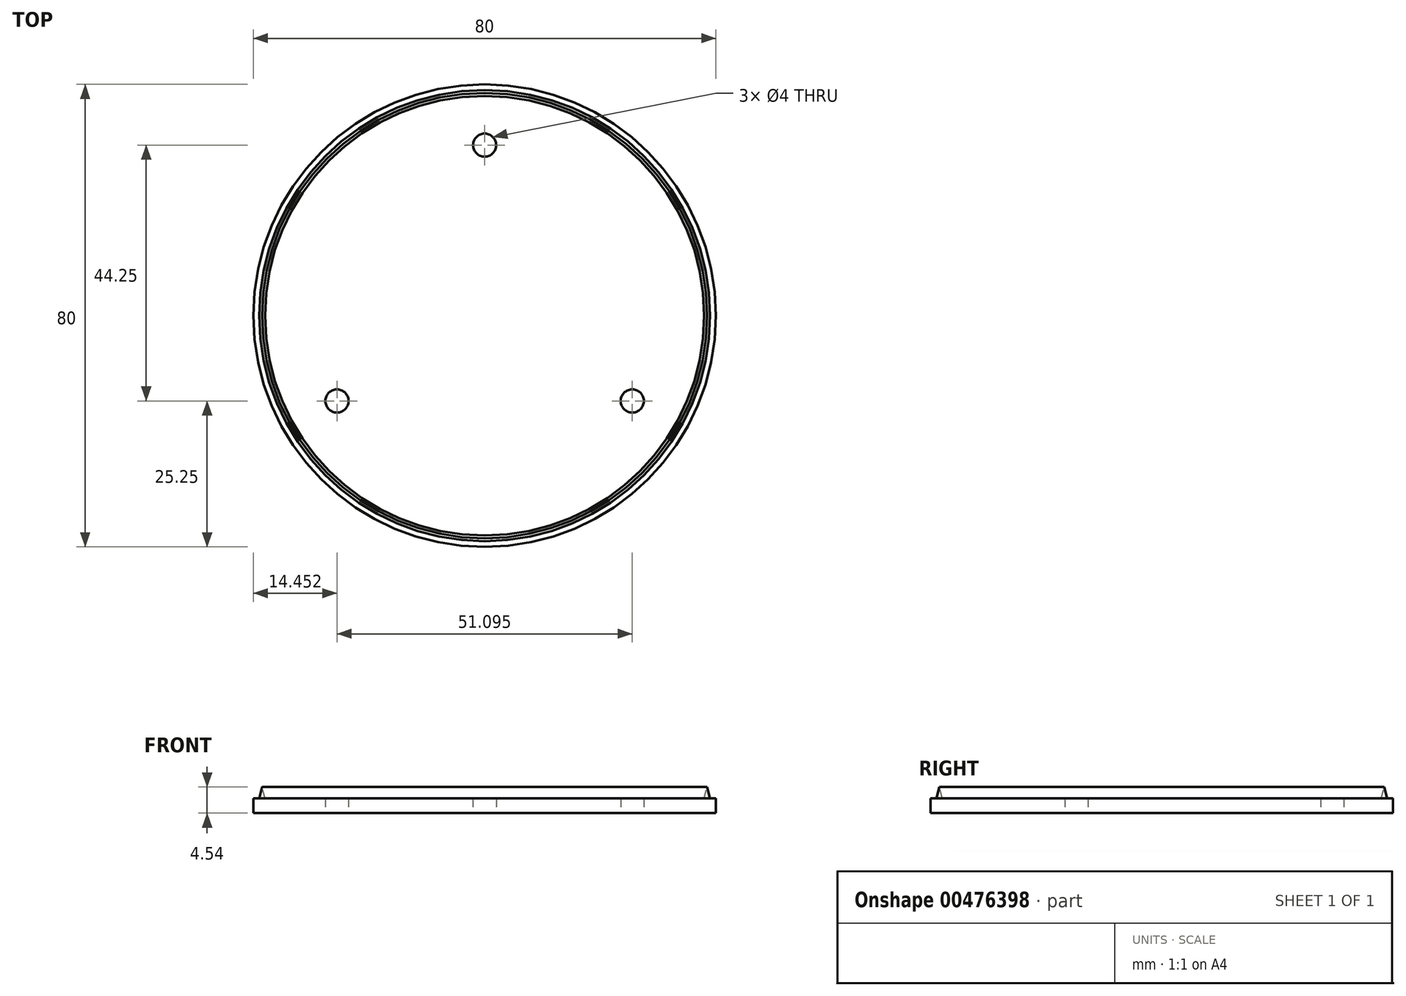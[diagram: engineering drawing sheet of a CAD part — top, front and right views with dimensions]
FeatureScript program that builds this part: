
annotation { "Feature Type Name" : "Feature", "Feature Type Description" : "" }
export const myFeature = defineFeature(function(context is Context, id is Id, definition is map)
    precondition{}
    {
        {
            var Q0;
            Q0=qCreatedBy(makeId("Top.planeOp"),FACE);
            var sketch = newSketch(context, id + "F0", { "sketchPlane" : qUnion([Q0])});
            skCircle(sketch, "E0", {"center": v(0, 0) * mm, "radius": 40 * mm});
            skCircle(sketch, "E1", {"center": v(0, 29.5) * mm, "radius": 2 * mm});
            skLineSegment(sketch, "E2", {"start": v(0, 0) * mm, "end": v(0, 29.5) * mm, "construction": true});
            skLineSegment(sketch, "E3.1.0", {"start": v(0, 0) * mm, "end": v(-25.55, -14.75) * mm, "construction": true});
            skCircle(sketch, "E3.1.1", {"center": v(-25.55, -14.75) * mm, "radius": 2 * mm});
            skLineSegment(sketch, "E3.2.0", {"start": v(0, 0) * mm, "end": v(25.55, -14.75) * mm, "construction": true});
            skCircle(sketch, "E3.2.1", {"center": v(25.55, -14.75) * mm, "radius": 2 * mm});
            skLineSegment(sketch, "E4", {"start": v(0, 29.5) * mm, "end": v(0, 40) * mm, "construction": true});
            skSolve(sketch);
        }
        {
            var Q0;
            Q0=makeQuery(id+"F0.imprint","IMPRINT",FACE,{"disambiguationData":[TD([[makeQuery(id+"F0.imprint","IMPRINT",EDGE,{"derivedFrom":sQuery(id+"F0.wireOp",EDGE,"E0")}),1.0]])]});
            extrude(context, id + "F1", {"entities" : qUnion([Q0]), "depth" : 2.54 * mm});
        }
        {
            var Q0;
            Q0=qCreatedBy(makeId("Front.planeOp"),FACE);
            var sketch = newSketch(context, id + "F2", { "sketchPlane" : qUnion([Q0])});
            skLineSegment(sketch, "E5", {"start": v(-39, 2.54) * mm, "end": v(-38.5, 4.54) * mm});
            skLineSegment(sketch, "E6", {"start": v(-38.5, 4.54) * mm, "end": v(-38, 2.54) * mm});
            skLineSegment(sketch, "E7", {"start": v(-38, 2.54) * mm, "end": v(-39, 2.54) * mm});
            skSolve(sketch);
        }
        {
            var Q0;
            Q0=qSketchRegion(id+"F2",true);
            var Q1;
            Q1=makeQuery(id+"F1.opExtrude","CAP_EDGE",EDGE,{"disambiguationData":[OSD([sQuery(id+"F0.wireOp",EDGE,"E0")])],"isStart":false});
            sweep(context, id + "F3", {"operationType" : NewBodyOperationType.ADD, "profiles" : qUnion([Q0]), "path" : qUnion([Q1])});
        }
    });
